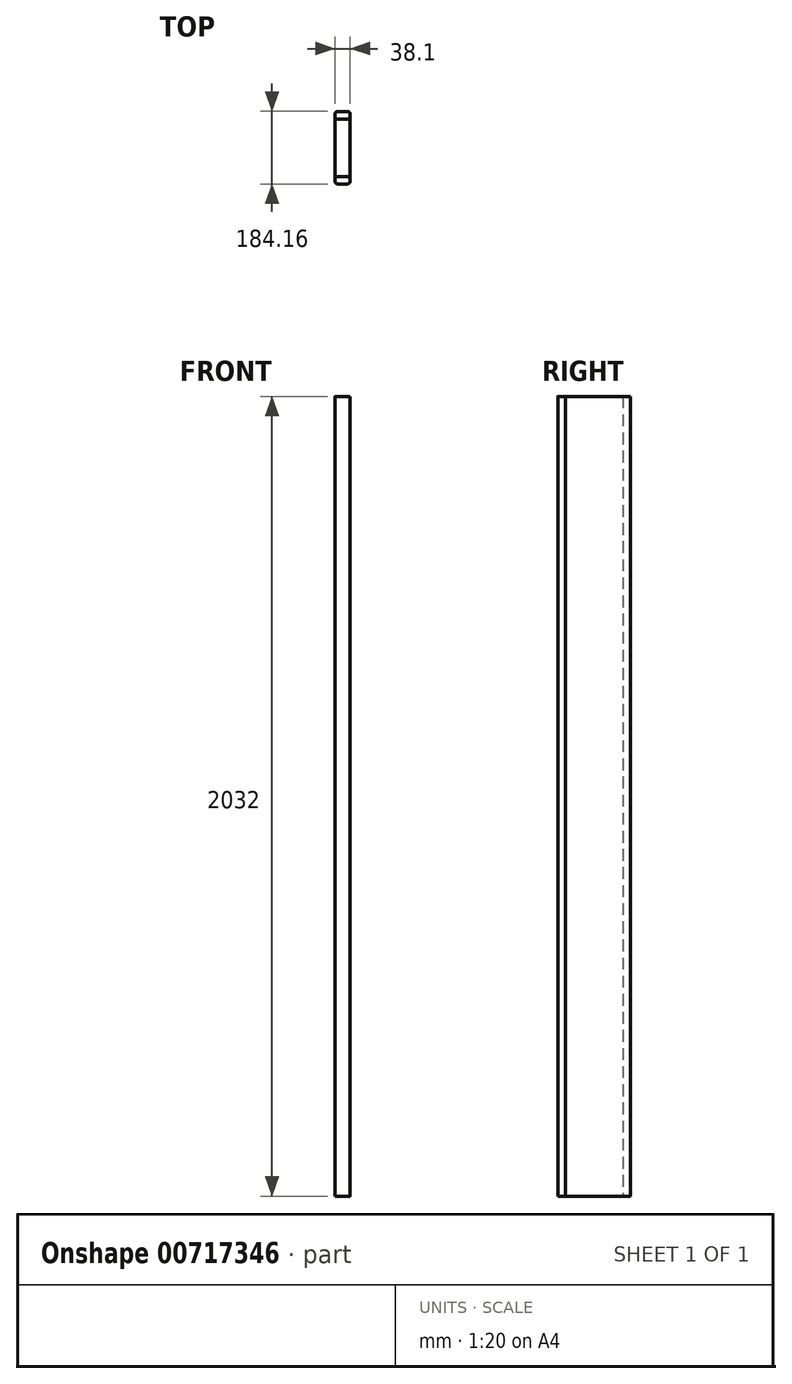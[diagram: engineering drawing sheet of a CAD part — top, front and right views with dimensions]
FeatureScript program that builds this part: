
annotation { "Feature Type Name" : "Feature", "Feature Type Description" : "" }
export const myFeature = defineFeature(function(context is Context, id is Id, definition is map)
    precondition{}
    {
        {
            var Q0;
            Q0=qCreatedBy(makeId("Top.planeOp"),FACE);
            var sketch = newSketch(context, id + "F0", { "sketchPlane" : qUnion([Q0])});
            skLineSegment(sketch, "E0.bottom", {"start": v(-12.7, 92.08) * mm, "end": v(12.7, 92.08) * mm});
            skLineSegment(sketch, "E0.top", {"start": v(-12.7, -92.08) * mm, "end": v(12.7, -92.08) * mm});
            skLineSegment(sketch, "E0.left", {"start": v(-19.05, 85.73) * mm, "end": v(-19.05, -85.73) * mm});
            skLineSegment(sketch, "E0.right", {"start": v(19.05, 85.73) * mm, "end": v(19.05, -85.73) * mm});
            skLineSegment(sketch, "E1", {"start": v(-19.05, -92.08) * mm, "end": v(19.05, 92.08) * mm, "construction": true});
            skPoint(sketch, "E2.visualSharp", {"position": v(19.05, 92.08) * mm});
            skArc(sketch, "E2.filletArc", {"start": v(19.05, 85.73) * mm, "mid": v(17.2, 90.22) * mm, "end": v(12.7, 92.08) * mm});
            skPoint(sketch, "E3.visualSharp", {"position": v(-19.05, 92.08) * mm});
            skArc(sketch, "E3.filletArc", {"start": v(-12.7, 92.08) * mm, "mid": v(-17.2, 90.22) * mm, "end": v(-19.05, 85.73) * mm});
            skPoint(sketch, "E4.visualSharp", {"position": v(-19.05, -92.08) * mm});
            skArc(sketch, "E4.filletArc", {"start": v(-19.05, -85.73) * mm, "mid": v(-17.2, -90.22) * mm, "end": v(-12.7, -92.08) * mm});
            skPoint(sketch, "E5.visualSharp", {"position": v(19.05, -92.08) * mm});
            skArc(sketch, "E5.filletArc", {"start": v(12.7, -92.08) * mm, "mid": v(17.2, -90.22) * mm, "end": v(19.05, -85.73) * mm});
            skSolve(sketch);
        }
        {
            var Q0;
            Q0=makeQuery(id+"F0.imprint","IMPRINT",FACE,{"disambiguationData":[TD([[makeQuery(id+"F0.imprint","IMPRINT",EDGE,{"derivedFrom":sQuery(id+"F0.wireOp",EDGE,"E0.bottom")}),-1.0]])]});
            extrude(context, id + "F1", {"entities" : qUnion([Q0]), "depth" : 2032 * mm, "offsetDistance" : 25.4 * mm});
        }
        {
            var Q0;
            Q0=qCreatedBy(makeId("Top.planeOp"),FACE);
            var sketch = newSketch(context, id + "F2", { "sketchPlane" : qUnion([Q0])});
            skLineSegment(sketch, "E6.bottom", {"start": v(-12.7, 73.03) * mm, "end": v(12.7, 73.03) * mm});
            skLineSegment(sketch, "E6.top", {"start": v(-19.05, -73.03) * mm, "end": v(19.05, -73.03) * mm});
            skLineSegment(sketch, "E6.left", {"start": v(-19.05, 66.68) * mm, "end": v(-19.05, -73.03) * mm});
            skLineSegment(sketch, "E6.right", {"start": v(19.05, 66.68) * mm, "end": v(19.05, -73.03) * mm});
            skLineSegment(sketch, "E7", {"start": v(-19.05, -73.03) * mm, "end": v(19.05, 73.03) * mm, "construction": true});
            skPoint(sketch, "E8.visualSharp", {"position": v(19.05, 73.03) * mm});
            skArc(sketch, "E8.filletArc", {"start": v(19.05, 66.68) * mm, "mid": v(17.2, 71.17) * mm, "end": v(12.7, 73.02) * mm});
            skPoint(sketch, "E9.visualSharp", {"position": v(-19.05, 73.03) * mm});
            skArc(sketch, "E9.filletArc", {"start": v(-12.7, 73.02) * mm, "mid": v(-17.2, 71.17) * mm, "end": v(-19.05, 66.68) * mm});
            skPoint(sketch, "E10.visualSharp", {"position": v(-19.05, -73.03) * mm});
            skPoint(sketch, "E11.visualSharp", {"position": v(19.05, -73.03) * mm});
            skSolve(sketch);
        }
        {
            var Q0;
            Q0=makeQuery(id+"F2.imprint","IMPRINT",FACE,{"disambiguationData":[TD([[makeQuery(id+"F2.imprint","IMPRINT",EDGE,{"derivedFrom":sQuery(id+"F2.wireOp",EDGE,"E6.bottom")}),-1.0]])]});
            extrude(context, id + "F3", {"entities" : qUnion([Q0]), "depth" : 2032 * mm, "offsetDistance" : 25.4 * mm});
        }
    });
